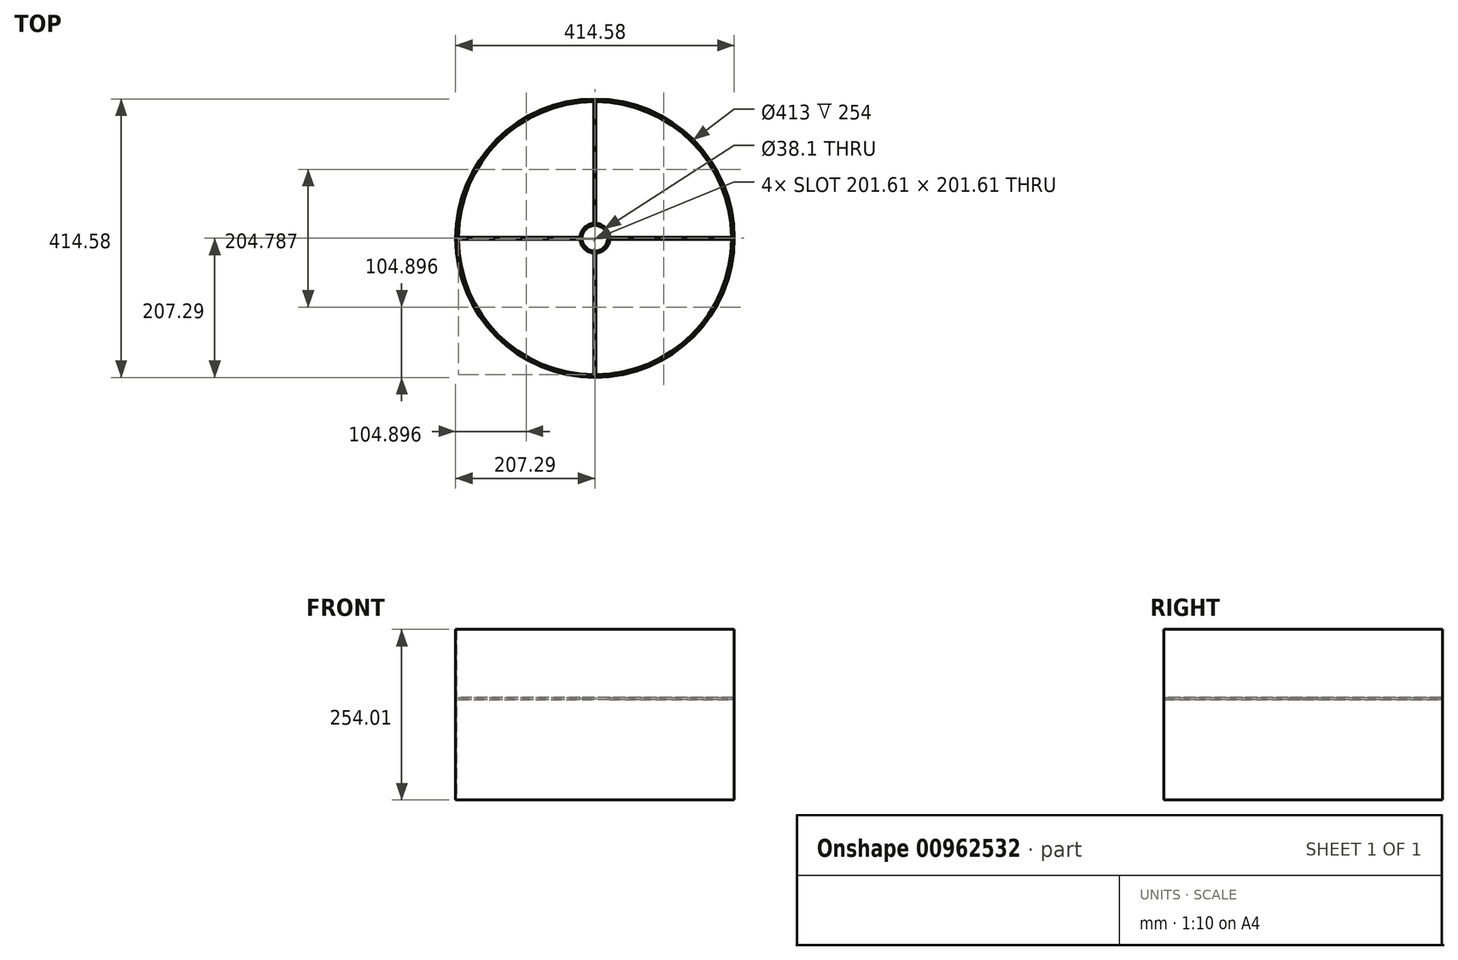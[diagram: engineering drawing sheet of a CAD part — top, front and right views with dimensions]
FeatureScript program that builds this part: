
annotation { "Feature Type Name" : "Feature", "Feature Type Description" : "" }
export const myFeature = defineFeature(function(context is Context, id is Id, definition is map)
    precondition{}
    {
        {
            var Q0;
            Q0=qCreatedBy(makeId("Top.planeOp"),FACE);
            var sketch = newSketch(context, id + "F0", { "sketchPlane" : qUnion([Q0])});
            skCircle(sketch, "E0", {"center": v(0, 0) * mm, "radius": 19.05 * mm});
            skLineSegment(sketch, "E1", {"start": v(0, 0) * mm, "end": v(0, 203.2) * mm, "construction": true});
            skLineSegment(sketch, "E2", {"start": v(0, 0) * mm, "end": v(0, -203.2) * mm, "construction": true});
            skLineSegment(sketch, "E3", {"start": v(0, 0) * mm, "end": v(203.2, 0) * mm, "construction": true});
            skLineSegment(sketch, "E4", {"start": v(0, 0) * mm, "end": v(-203.2, 0) * mm, "construction": true});
            skLineSegment(sketch, "E5", {"start": v(22.17, 1.59) * mm, "end": v(203.2, 1.59) * mm});
            skLineSegment(sketch, "E6", {"start": v(203.2, -1.59) * mm, "end": v(22.17, -1.59) * mm});
            skLineSegment(sketch, "E7", {"start": v(1.59, 22.17) * mm, "end": v(1.59, 203.2) * mm});
            skLineSegment(sketch, "E8", {"start": v(-1.59, 203.2) * mm, "end": v(-1.59, 22.17) * mm});
            skLineSegment(sketch, "E9", {"start": v(-22.17, 1.59) * mm, "end": v(-203.2, 1.59) * mm});
            skLineSegment(sketch, "E10", {"start": v(-22.17, -1.59) * mm, "end": v(-203.2, -1.59) * mm});
            skLineSegment(sketch, "E11", {"start": v(-1.59, -22.17) * mm, "end": v(-1.59, -203.2) * mm});
            skLineSegment(sketch, "E12", {"start": v(1.59, -203.2) * mm, "end": v(1.59, -22.17) * mm});
            skArc(sketch, "E13", {"start": v(22.17, 1.59) * mm, "mid": v(15.72, 15.72) * mm, "end": v(1.59, 22.17) * mm});
            skArc(sketch, "E14", {"start": v(-1.59, 22.17) * mm, "mid": v(-15.72, 15.72) * mm, "end": v(-22.17, 1.59) * mm});
            skArc(sketch, "E15", {"start": v(-22.17, -1.59) * mm, "mid": v(-15.72, -15.72) * mm, "end": v(-1.59, -22.17) * mm});
            skArc(sketch, "E16", {"start": v(1.59, -22.17) * mm, "mid": v(15.72, -15.72) * mm, "end": v(22.17, -1.59) * mm});
            skArc(sketch, "E17", {"start": v(-203.2, 1.59) * mm, "mid": v(-143.69, 143.69) * mm, "end": v(-1.59, 203.2) * mm});
            skArc(sketch, "E18", {"start": v(1.59, 203.2) * mm, "mid": v(143.69, 143.69) * mm, "end": v(203.2, 1.59) * mm});
            skArc(sketch, "E19", {"start": v(-1.59, -203.2) * mm, "mid": v(-143.69, -143.69) * mm, "end": v(-203.2, -1.59) * mm});
            skCircle(sketch, "E20", {"center": v(0, 0) * mm, "radius": 206.5 * mm});
            skArc(sketch, "E21", {"start": v(203.2, -1.59) * mm, "mid": v(143.69, -143.69) * mm, "end": v(1.59, -203.2) * mm});
            skSolve(sketch);
        }
        {
            var Q0;
            Q0=makeQuery(id+"F0.imprint","IMPRINT",FACE,{"disambiguationData":[TD([[makeQuery(id+"F0.imprint","IMPRINT",EDGE,{"derivedFrom":sQuery(id+"F0.wireOp",EDGE,"E0")}),-1.0]])]});
            extrude(context, id + "F1", {"entities" : qUnion([Q0]), "depth" : 3.17 * mm, "offsetDistance" : 25.4 * mm});
        }
        {
            var Q0;
            Q0=makeQuery(id+"F1.opExtrude","CAP_FACE",FACE,{"disambiguationData":[OSD([sQuery(id+"F0.wireOp",EDGE,"E0"),sQuery(id+"F0.wireOp",EDGE,"E5"),sQuery(id+"F0.wireOp",EDGE,"E6"),sQuery(id+"F0.wireOp",EDGE,"E7"),sQuery(id+"F0.wireOp",EDGE,"E8"),sQuery(id+"F0.wireOp",EDGE,"E9"),sQuery(id+"F0.wireOp",EDGE,"E10"),sQuery(id+"F0.wireOp",EDGE,"E11"),sQuery(id+"F0.wireOp",EDGE,"E12"),sQuery(id+"F0.wireOp",EDGE,"E13"),sQuery(id+"F0.wireOp",EDGE,"E14"),sQuery(id+"F0.wireOp",EDGE,"E15"),sQuery(id+"F0.wireOp",EDGE,"E16"),sQuery(id+"F0.wireOp",EDGE,"E17"),sQuery(id+"F0.wireOp",EDGE,"E18"),sQuery(id+"F0.wireOp",EDGE,"E19"),sQuery(id+"F0.wireOp",EDGE,"E20"),sQuery(id+"F0.wireOp",EDGE,"E21")])],"isStart":false});
            var sketch = newSketch(context, id + "F2", { "sketchPlane" : qUnion([Q0])});
            skCircle(sketch, "E22.0", {"center": v(0, 0) * mm, "radius": 206.5 * mm});
            skLineSegment(sketch, "E23", {"start": v(0, 0) * mm, "end": v(206.5, 0) * mm, "construction": true});
            skCircle(sketch, "E24", {"center": v(0, 0) * mm, "radius": 207.3 * mm});
            skSolve(sketch);
        }
        {
            var Q0;
            Q0 = qSketchRegion(id + "F2", true);
            extrude(context, id + "F3", {"entities" : qUnion([Q0]), "depth" : 101.6 * mm, "offsetDistance" : 25.4 * mm, "hasSecondDirection" : true, "secondDirectionOppositeDirection" : true, "secondDirectionDepth" : 152.4 * mm});
        }
    });
